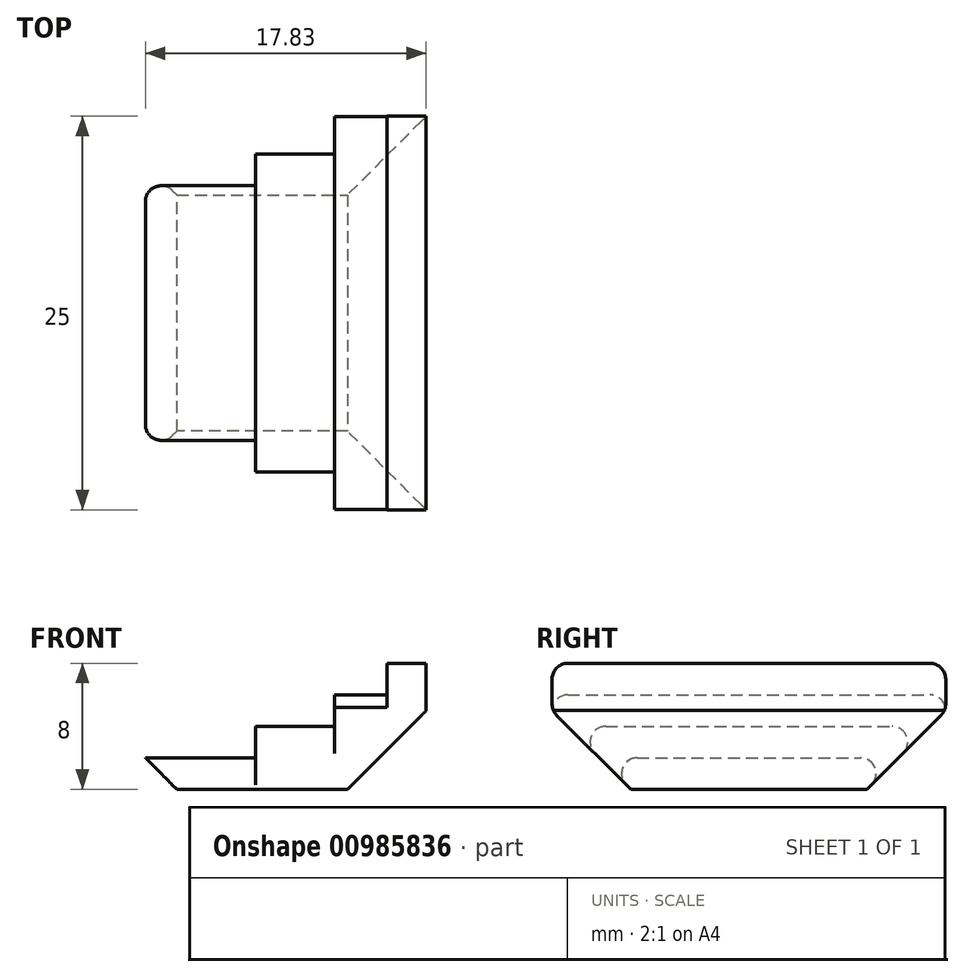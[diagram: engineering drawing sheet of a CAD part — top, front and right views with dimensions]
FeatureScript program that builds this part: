
annotation { "Feature Type Name" : "Feature", "Feature Type Description" : "" }
export const myFeature = defineFeature(function(context is Context, id is Id, definition is map)
    precondition{}
    {
        {
            assignVariable(context, id + "F0", {"name" : "total_length", "anyValue" : 25 * mm});
        }
        {
            var Q0;
            Q0=qCreatedBy(makeId("Front.planeOp"),FACE);
            var sketch = newSketch(context, id + "F1", { "sketchPlane" : qUnion([Q0])});
            skLineSegment(sketch, "E0", {"start": v(0, 0) * mm, "end": v(0, 2) * mm});
            skLineSegment(sketch, "E1", {"start": v(0, 2) * mm, "end": v(10, 2) * mm});
            skLineSegment(sketch, "E2", {"start": v(10, 2) * mm, "end": v(10, 4) * mm});
            skLineSegment(sketch, "E3", {"start": v(10, 4) * mm, "end": v(15, 4) * mm});
            skLineSegment(sketch, "E4", {"start": v(15, 4) * mm, "end": v(15, 6) * mm});
            skLineSegment(sketch, "E5", {"start": v(15, 6) * mm, "end": v(18.33, 6) * mm});
            skLineSegment(sketch, "E6", {"start": v(20.83, 0) * mm, "end": v(0, 0) * mm});
            skLineSegment(sketch, "E7", {"start": v(20.83, 0) * mm, "end": v(20.83, 8) * mm});
            skLineSegment(sketch, "E8", {"start": v(20.83, 8) * mm, "end": v(18.33, 8) * mm});
            skLineSegment(sketch, "E9", {"start": v(18.33, 8) * mm, "end": v(18.33, 6) * mm});
            skSolve(sketch);
        }
        {
            var Q0;
            Q0=makeQuery(id+"F1.imprint","IMPRINT",FACE,{"disambiguationData":[TD([[makeQuery(id+"F1.imprint","IMPRINT",EDGE,{"derivedFrom":sQuery(id+"F1.wireOp",EDGE,"E0")}),-1.0]])]});
            extrude(context, id + "F2", {"entities" : qUnion([Q0]), "depth" : getVariable(context, 'total_length'), "offsetDistance" : 25 * mm, "symmetric" : true});
        }
        {
            var Q0;
            Q0=makeQuery(id+"F2.opExtrude","CAP_EDGE",EDGE,{"disambiguationData":[OSD([sQuery(id+"F1.wireOp",EDGE,"E6")])],"isStart":false});
            var Q1;
            Q1=makeQuery(id+"F2.opExtrude","SWEPT_EDGE",EDGE,{"disambiguationData":[OSD([sQuery(id+"F1.wireOp",EDGE,"E0"),sQuery(id+"F1.wireOp",EDGE,"E6")])]});
            var Q2;
            Q2=makeQuery(id+"F2.opExtrude","CAP_EDGE",EDGE,{"disambiguationData":[OSD([sQuery(id+"F1.wireOp",EDGE,"E6")])],"isStart":true});
            var Q3;
            Q3=makeQuery(id+"F2.opExtrude","SWEPT_EDGE",EDGE,{"disambiguationData":[OSD([sQuery(id+"F1.wireOp",EDGE,"E6"),sQuery(id+"F1.wireOp",EDGE,"E7")])]});
            chamfer(context, id + "F3", {"entities" : qUnion([Q0, Q1, Q2, Q3]), "width" : 5 * mm, "tangentPropagation" : true});
        }
        {
            var Q0;
            Q0=makeQuery(id+"F3.opChamfer","BLEND_EDGE",EDGE,{"blendedFrom":[makeQuery(id+"F2.opExtrude","CAP_EDGE",EDGE,{"disambiguationData":[OSD([sQuery(id+"F1.wireOp",EDGE,"E6")])],"isStart":false}),makeQuery(id+"F2.opExtrude","SWEPT_FACE",FACE,{"disambiguationData":[OSD([sQuery(id+"F1.wireOp",EDGE,"E1")])]})],"blendedInto":[makeQuery(id+"F2.opExtrude","SWEPT_FACE",FACE,{"disambiguationData":[OSD([sQuery(id+"F1.wireOp",EDGE,"E1")])]})]});
            var Q1;
            Q1=makeQuery(id+"F3.opChamfer","BLEND_EDGE",EDGE,{"blendedFrom":[makeQuery(id+"F2.opExtrude","CAP_EDGE",EDGE,{"disambiguationData":[OSD([sQuery(id+"F1.wireOp",EDGE,"E6")])],"isStart":false}),makeQuery(id+"F2.opExtrude","SWEPT_FACE",FACE,{"disambiguationData":[OSD([sQuery(id+"F1.wireOp",EDGE,"E3")])]})],"blendedInto":[makeQuery(id+"F2.opExtrude","SWEPT_FACE",FACE,{"disambiguationData":[OSD([sQuery(id+"F1.wireOp",EDGE,"E3")])]})]});
            var Q2;
            Q2=makeQuery(id+"F2.opExtrude","CAP_EDGE",EDGE,{"disambiguationData":[OSD([sQuery(id+"F1.wireOp",EDGE,"E5")])],"isStart":false});
            var Q3;
            Q3=makeQuery(id+"F2.opExtrude","CAP_EDGE",EDGE,{"disambiguationData":[OSD([sQuery(id+"F1.wireOp",EDGE,"E8")])],"isStart":false});
            var Q4;
            Q4=makeQuery(id+"F2.opExtrude","CAP_EDGE",EDGE,{"disambiguationData":[OSD([sQuery(id+"F1.wireOp",EDGE,"E8")])],"isStart":true});
            var Q5;
            Q5=makeQuery(id+"F2.opExtrude","CAP_EDGE",EDGE,{"disambiguationData":[OSD([sQuery(id+"F1.wireOp",EDGE,"E5")])],"isStart":true});
            var Q6;
            Q6=makeQuery(id+"F3.opChamfer","BLEND_EDGE",EDGE,{"blendedFrom":[makeQuery(id+"F2.opExtrude","CAP_EDGE",EDGE,{"disambiguationData":[OSD([sQuery(id+"F1.wireOp",EDGE,"E6")])],"isStart":true}),makeQuery(id+"F2.opExtrude","SWEPT_FACE",FACE,{"disambiguationData":[OSD([sQuery(id+"F1.wireOp",EDGE,"E3")])]})],"blendedInto":[makeQuery(id+"F2.opExtrude","SWEPT_FACE",FACE,{"disambiguationData":[OSD([sQuery(id+"F1.wireOp",EDGE,"E3")])]})]});
            var Q7;
            Q7=makeQuery(id+"F3.opChamfer","BLEND_EDGE",EDGE,{"blendedFrom":[makeQuery(id+"F2.opExtrude","CAP_EDGE",EDGE,{"disambiguationData":[OSD([sQuery(id+"F1.wireOp",EDGE,"E6")])],"isStart":true}),makeQuery(id+"F2.opExtrude","SWEPT_FACE",FACE,{"disambiguationData":[OSD([sQuery(id+"F1.wireOp",EDGE,"E1")])]})],"blendedInto":[makeQuery(id+"F2.opExtrude","SWEPT_FACE",FACE,{"disambiguationData":[OSD([sQuery(id+"F1.wireOp",EDGE,"E1")])]})]});
            var Q8;
            {var subQ0=sQuery(id+"F1.wireOp",EDGE,"E6");Q8=makeQuery(id+"F3.opChamfer","BLEND_EDGE",EDGE,{"blendedFrom":[makeQuery(id+"F2.opExtrude","CAP_EDGE",EDGE,{"disambiguationData":[OSD([subQ0])],"isStart":false}),makeQuery(id+"F2.opExtrude","CAP_FACE",FACE,{"disambiguationData":[OSD([sQuery(id+"F1.wireOp",EDGE,"E0"),sQuery(id+"F1.wireOp",EDGE,"E1"),sQuery(id+"F1.wireOp",EDGE,"E2"),sQuery(id+"F1.wireOp",EDGE,"E3"),sQuery(id+"F1.wireOp",EDGE,"E4"),sQuery(id+"F1.wireOp",EDGE,"E5"),subQ0,sQuery(id+"F1.wireOp",EDGE,"E7"),sQuery(id+"F1.wireOp",EDGE,"E8"),sQuery(id+"F1.wireOp",EDGE,"E9")])],"isStart":false})],"blendedInto":[makeQuery(id+"F2.opExtrude","CAP_FACE",FACE,{"disambiguationData":[OSD([sQuery(id+"F1.wireOp",EDGE,"E0"),sQuery(id+"F1.wireOp",EDGE,"E1"),sQuery(id+"F1.wireOp",EDGE,"E2"),sQuery(id+"F1.wireOp",EDGE,"E3"),sQuery(id+"F1.wireOp",EDGE,"E4"),sQuery(id+"F1.wireOp",EDGE,"E5"),subQ0,sQuery(id+"F1.wireOp",EDGE,"E7"),sQuery(id+"F1.wireOp",EDGE,"E8"),sQuery(id+"F1.wireOp",EDGE,"E9")])],"isStart":false})]});}
            var Q9;
            {var subQ0=sQuery(id+"F1.wireOp",EDGE,"E6");Q9=makeQuery(id+"F3.opChamfer","BLEND_EDGE",EDGE,{"blendedFrom":[makeQuery(id+"F2.opExtrude","CAP_EDGE",EDGE,{"disambiguationData":[OSD([subQ0])],"isStart":true}),makeQuery(id+"F2.opExtrude","CAP_FACE",FACE,{"disambiguationData":[OSD([sQuery(id+"F1.wireOp",EDGE,"E0"),sQuery(id+"F1.wireOp",EDGE,"E1"),sQuery(id+"F1.wireOp",EDGE,"E2"),sQuery(id+"F1.wireOp",EDGE,"E3"),sQuery(id+"F1.wireOp",EDGE,"E4"),sQuery(id+"F1.wireOp",EDGE,"E5"),subQ0,sQuery(id+"F1.wireOp",EDGE,"E7"),sQuery(id+"F1.wireOp",EDGE,"E8"),sQuery(id+"F1.wireOp",EDGE,"E9")])],"isStart":true})],"blendedInto":[makeQuery(id+"F2.opExtrude","CAP_FACE",FACE,{"disambiguationData":[OSD([sQuery(id+"F1.wireOp",EDGE,"E0"),sQuery(id+"F1.wireOp",EDGE,"E1"),sQuery(id+"F1.wireOp",EDGE,"E2"),sQuery(id+"F1.wireOp",EDGE,"E3"),sQuery(id+"F1.wireOp",EDGE,"E4"),sQuery(id+"F1.wireOp",EDGE,"E5"),subQ0,sQuery(id+"F1.wireOp",EDGE,"E7"),sQuery(id+"F1.wireOp",EDGE,"E8"),sQuery(id+"F1.wireOp",EDGE,"E9")])],"isStart":true})]});}
            fillet(context, id + "F4", {"entities" : qUnion([Q0, Q1, Q2, Q3, Q4, Q5, Q6, Q7, Q8, Q9]), "radius" : 1 * mm, "tangentPropagation" : true, "allowEdgeOverflow" : false});
        }
    });
